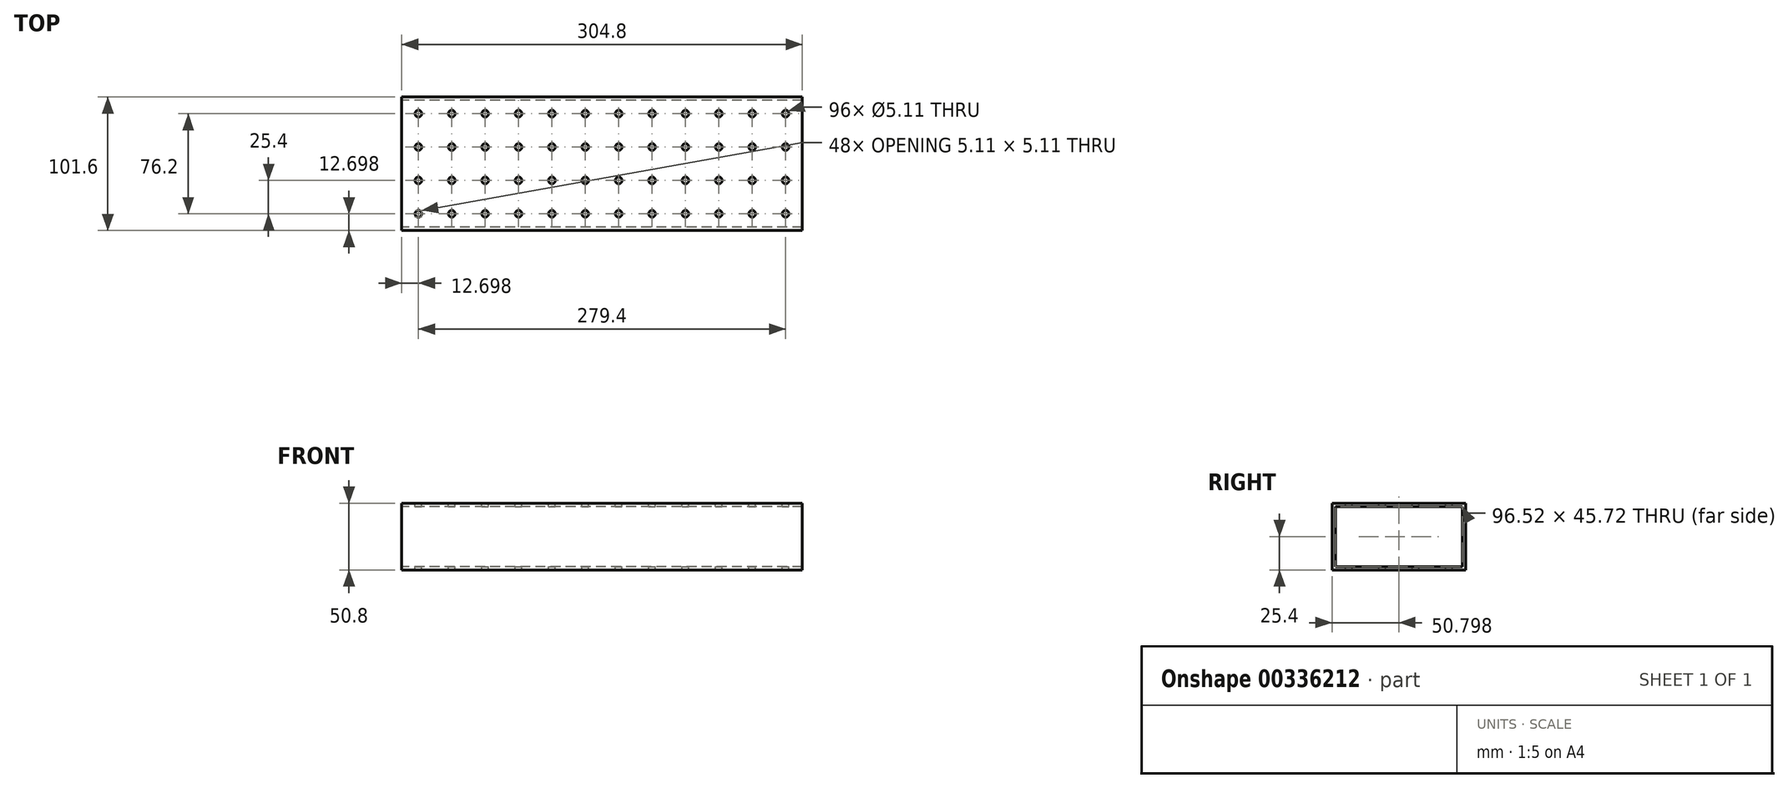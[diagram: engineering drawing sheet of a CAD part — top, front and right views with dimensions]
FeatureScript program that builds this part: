
annotation { "Feature Type Name" : "Feature", "Feature Type Description" : "" }
export const myFeature = defineFeature(function(context is Context, id is Id, definition is map)
    precondition{}
    {
        {
            var Q0;
            Q0=qCreatedBy(makeId("Top.planeOp"),FACE);
            var sketch = newSketch(context, id + "F0", { "sketchPlane" : qUnion([Q0])});
            skLineSegment(sketch, "E0.bottom", {"start": v(-146.87, 30.52) * mm, "end": v(157.93, 30.52) * mm});
            skLineSegment(sketch, "E0.top", {"start": v(-146.87, -71.08) * mm, "end": v(157.93, -71.08) * mm});
            skLineSegment(sketch, "E0.left", {"start": v(-146.87, 30.52) * mm, "end": v(-146.87, -71.08) * mm});
            skLineSegment(sketch, "E0.right", {"start": v(157.93, 30.52) * mm, "end": v(157.93, -71.08) * mm});
            skSolve(sketch);
        }
        {
            var Q0;
            Q0 = qSketchRegion(id + "F0", true);
            extrude(context, id + "F1", {"entities" : qUnion([Q0]), "depth" : 50.8 * mm});
        }
        {
            var Q0;
            Q0=makeQuery(id+"F1.opExtrude","SWEPT_FACE",FACE,{"disambiguationData":[OSD([sQuery(id+"F0.wireOp",EDGE,"E0.left")])]});
            var sketch = newSketch(context, id + "F2", { "sketchPlane" : qUnion([Q0])});
            skLineSegment(sketch, "E1.bottom", {"start": v(-27.98, 48.26) * mm, "end": v(68.54, 48.26) * mm});
            skLineSegment(sketch, "E1.top", {"start": v(-27.98, 2.54) * mm, "end": v(68.54, 2.54) * mm});
            skLineSegment(sketch, "E1.left", {"start": v(-27.98, 48.26) * mm, "end": v(-27.98, 2.54) * mm});
            skLineSegment(sketch, "E1.right", {"start": v(68.54, 48.26) * mm, "end": v(68.54, 2.54) * mm});
            skSolve(sketch);
        }
        {
            var Q0;
            Q0 = qSketchRegion(id + "F2", true);
            extrude(context, id + "F3", {"entities" : qUnion([Q0]), "operationType" : NewBodyOperationType.REMOVE, "endBound" : BoundingType.THROUGH_ALL, "oppositeDirection" : true, "depth" : 25.4 * mm});
        }
        {
            var Q0;
            Q0=makeQuery(id+"F1.opExtrude","CAP_FACE",FACE,{"disambiguationData":[OSD([sQuery(id+"F0.wireOp",EDGE,"E0.bottom"),sQuery(id+"F0.wireOp",EDGE,"E0.top"),sQuery(id+"F0.wireOp",EDGE,"E0.left"),sQuery(id+"F0.wireOp",EDGE,"E0.right")])],"isStart":false});
            var sketch = newSketch(context, id + "F4", { "sketchPlane" : qUnion([Q0])});
            skCircle(sketch, "E2", {"center": v(-134.17, 17.82) * mm, "radius": 2.55 * mm});
            skCircle(sketch, "E3.0.1.0", {"center": v(-134.17, -7.58) * mm, "radius": 2.55 * mm});
            skCircle(sketch, "E3.0.2.0", {"center": v(-134.17, -32.98) * mm, "radius": 2.55 * mm});
            skCircle(sketch, "E3.0.3.0", {"center": v(-134.17, -58.38) * mm, "radius": 2.55 * mm});
            skCircle(sketch, "E3.1.0.0", {"center": v(-108.77, 17.82) * mm, "radius": 2.55 * mm});
            skCircle(sketch, "E3.1.1.0", {"center": v(-108.77, -7.58) * mm, "radius": 2.55 * mm});
            skCircle(sketch, "E3.1.2.0", {"center": v(-108.77, -32.98) * mm, "radius": 2.55 * mm});
            skCircle(sketch, "E3.1.3.0", {"center": v(-108.77, -58.38) * mm, "radius": 2.55 * mm});
            skCircle(sketch, "E3.2.0.0", {"center": v(-83.37, 17.82) * mm, "radius": 2.55 * mm});
            skCircle(sketch, "E3.2.1.0", {"center": v(-83.37, -7.58) * mm, "radius": 2.55 * mm});
            skCircle(sketch, "E3.2.2.0", {"center": v(-83.37, -32.98) * mm, "radius": 2.55 * mm});
            skCircle(sketch, "E3.2.3.0", {"center": v(-83.37, -58.38) * mm, "radius": 2.55 * mm});
            skCircle(sketch, "E3.3.0.0", {"center": v(-57.97, 17.82) * mm, "radius": 2.55 * mm});
            skCircle(sketch, "E3.3.1.0", {"center": v(-57.97, -7.58) * mm, "radius": 2.55 * mm});
            skCircle(sketch, "E3.3.2.0", {"center": v(-57.97, -32.98) * mm, "radius": 2.55 * mm});
            skCircle(sketch, "E3.3.3.0", {"center": v(-57.97, -58.38) * mm, "radius": 2.55 * mm});
            skCircle(sketch, "E3.4.0.0", {"center": v(-32.57, 17.82) * mm, "radius": 2.55 * mm});
            skCircle(sketch, "E3.4.1.0", {"center": v(-32.57, -7.58) * mm, "radius": 2.55 * mm});
            skCircle(sketch, "E3.4.2.0", {"center": v(-32.57, -32.98) * mm, "radius": 2.55 * mm});
            skCircle(sketch, "E3.4.3.0", {"center": v(-32.57, -58.38) * mm, "radius": 2.55 * mm});
            skCircle(sketch, "E3.5.0.0", {"center": v(-7.17, 17.82) * mm, "radius": 2.55 * mm});
            skCircle(sketch, "E3.5.1.0", {"center": v(-7.17, -7.58) * mm, "radius": 2.55 * mm});
            skCircle(sketch, "E3.5.2.0", {"center": v(-7.17, -32.98) * mm, "radius": 2.55 * mm});
            skCircle(sketch, "E3.5.3.0", {"center": v(-7.17, -58.38) * mm, "radius": 2.55 * mm});
            skCircle(sketch, "E3.6.0.0", {"center": v(18.23, 17.82) * mm, "radius": 2.55 * mm});
            skCircle(sketch, "E3.6.1.0", {"center": v(18.23, -7.58) * mm, "radius": 2.55 * mm});
            skCircle(sketch, "E3.6.2.0", {"center": v(18.23, -32.98) * mm, "radius": 2.55 * mm});
            skCircle(sketch, "E3.6.3.0", {"center": v(18.23, -58.38) * mm, "radius": 2.55 * mm});
            skCircle(sketch, "E3.7.0.0", {"center": v(43.63, 17.82) * mm, "radius": 2.55 * mm});
            skCircle(sketch, "E3.7.1.0", {"center": v(43.63, -7.58) * mm, "radius": 2.55 * mm});
            skCircle(sketch, "E3.7.2.0", {"center": v(43.63, -32.98) * mm, "radius": 2.55 * mm});
            skCircle(sketch, "E3.7.3.0", {"center": v(43.63, -58.38) * mm, "radius": 2.55 * mm});
            skCircle(sketch, "E3.8.0.0", {"center": v(69.03, 17.82) * mm, "radius": 2.55 * mm});
            skCircle(sketch, "E3.8.1.0", {"center": v(69.03, -7.58) * mm, "radius": 2.55 * mm});
            skCircle(sketch, "E3.8.2.0", {"center": v(69.03, -32.98) * mm, "radius": 2.55 * mm});
            skCircle(sketch, "E3.8.3.0", {"center": v(69.03, -58.38) * mm, "radius": 2.55 * mm});
            skCircle(sketch, "E3.9.0.0", {"center": v(94.43, 17.82) * mm, "radius": 2.55 * mm});
            skCircle(sketch, "E3.9.1.0", {"center": v(94.43, -7.58) * mm, "radius": 2.55 * mm});
            skCircle(sketch, "E3.9.2.0", {"center": v(94.43, -32.98) * mm, "radius": 2.55 * mm});
            skCircle(sketch, "E3.9.3.0", {"center": v(94.43, -58.38) * mm, "radius": 2.55 * mm});
            skCircle(sketch, "E3.10.0.0", {"center": v(119.83, 17.82) * mm, "radius": 2.55 * mm});
            skCircle(sketch, "E3.10.1.0", {"center": v(119.83, -7.58) * mm, "radius": 2.55 * mm});
            skCircle(sketch, "E3.10.2.0", {"center": v(119.83, -32.98) * mm, "radius": 2.55 * mm});
            skCircle(sketch, "E3.10.3.0", {"center": v(119.83, -58.38) * mm, "radius": 2.55 * mm});
            skCircle(sketch, "E3.11.0.0", {"center": v(145.23, 17.82) * mm, "radius": 2.55 * mm});
            skCircle(sketch, "E3.11.1.0", {"center": v(145.23, -7.58) * mm, "radius": 2.55 * mm});
            skCircle(sketch, "E3.11.2.0", {"center": v(145.23, -32.98) * mm, "radius": 2.55 * mm});
            skCircle(sketch, "E3.11.3.0", {"center": v(145.23, -58.38) * mm, "radius": 2.55 * mm});
            skLineSegment(sketch, "E3.direction1", {"start": v(-134.17, 17.82) * mm, "end": v(-108.77, 17.82) * mm, "construction": true});
            skLineSegment(sketch, "E3.direction2", {"start": v(-134.17, 17.82) * mm, "end": v(-134.17, -7.58) * mm, "construction": true});
            skSolve(sketch);
        }
        {
            var Q0;
            Q0=sQuery(id+"F4.wireOp",VERTEX,"E3.11.3.0.center");
            var Q1;
            Q1=sQuery(id+"F4.wireOp",VERTEX,"E3.7.3.0.center");
            var Q2;
            Q2=sQuery(id+"F4.wireOp",VERTEX,"E3.3.3.0.center");
            var Q3;
            Q3=sQuery(id+"F4.wireOp",VERTEX,"E3.9.2.0.center");
            var Q4;
            Q4=sQuery(id+"F4.wireOp",VERTEX,"E3.5.2.0.center");
            var Q5;
            Q5=sQuery(id+"F4.wireOp",VERTEX,"E3.10.1.0.center");
            var Q6;
            Q6=sQuery(id+"F4.wireOp",VERTEX,"E3.8.0.0.center");
            var Q7;
            Q7=sQuery(id+"F4.wireOp",VERTEX,"E3.6.1.0.center");
            var Q8;
            Q8=sQuery(id+"F4.wireOp",VERTEX,"E3.4.0.0.center");
            var Q9;
            Q9=sQuery(id+"F4.wireOp",VERTEX,"E3.8.3.0.center");
            var Q10;
            Q10=sQuery(id+"F4.wireOp",VERTEX,"E3.4.3.0.center");
            var Q11;
            Q11=sQuery(id+"F4.wireOp",VERTEX,"E3.11.0.0.center");
            var Q12;
            Q12=sQuery(id+"F4.wireOp",VERTEX,"E3.7.0.0.center");
            var Q13;
            Q13=sQuery(id+"F4.wireOp",VERTEX,"E3.3.0.0.center");
            var Q14;
            Q14=sQuery(id+"F4.wireOp",VERTEX,"E3.9.3.0.center");
            var Q15;
            Q15=sQuery(id+"F4.wireOp",VERTEX,"E3.5.3.0.center");
            var Q16;
            Q16=sQuery(id+"F4.wireOp",VERTEX,"E3.10.2.0.center");
            var Q17;
            Q17=sQuery(id+"F4.wireOp",VERTEX,"E3.8.1.0.center");
            var Q18;
            Q18=sQuery(id+"F4.wireOp",VERTEX,"E3.6.2.0.center");
            var Q19;
            Q19=sQuery(id+"F4.wireOp",VERTEX,"E3.4.1.0.center");
            var Q20;
            Q20=sQuery(id+"F4.wireOp",VERTEX,"E3.11.1.0.center");
            var Q21;
            Q21=sQuery(id+"F4.wireOp",VERTEX,"E3.7.1.0.center");
            var Q22;
            Q22=sQuery(id+"F4.wireOp",VERTEX,"E3.3.1.0.center");
            var Q23;
            Q23=sQuery(id+"F4.wireOp",VERTEX,"E3.10.0.0.center");
            var Q24;
            Q24=sQuery(id+"F4.wireOp",VERTEX,"E3.2.1.0.center");
            var Q25;
            Q25=sQuery(id+"F4.wireOp",VERTEX,"E3.6.0.0.center");
            var Q26;
            Q26=sQuery(id+"F4.wireOp",VERTEX,"E3.2.2.0.center");
            var Q27;
            Q27=sQuery(id+"F4.wireOp",VERTEX,"E3.2.3.0.center");
            var Q28;
            Q28=sQuery(id+"F4.wireOp",VERTEX,"E3.9.0.0.center");
            var Q29;
            Q29=sQuery(id+"F4.wireOp",VERTEX,"E3.5.0.0.center");
            var Q30;
            Q30=sQuery(id+"F4.wireOp",VERTEX,"E2.center");
            var Q31;
            Q31=sQuery(id+"F4.wireOp",VERTEX,"E3.10.3.0.center");
            var Q32;
            Q32=sQuery(id+"F4.wireOp",VERTEX,"E3.6.3.0.center");
            var Q33;
            Q33=sQuery(id+"F4.wireOp",VERTEX,"E3.8.2.0.center");
            var Q34;
            Q34=sQuery(id+"F4.wireOp",VERTEX,"E3.4.2.0.center");
            var Q35;
            Q35=sQuery(id+"F4.wireOp",VERTEX,"E3.0.1.0.center");
            var Q36;
            Q36=sQuery(id+"F4.wireOp",VERTEX,"E3.0.2.0.center");
            var Q37;
            Q37=sQuery(id+"F4.wireOp",VERTEX,"E3.11.2.0.center");
            var Q38;
            Q38=sQuery(id+"F4.wireOp",VERTEX,"E3.7.2.0.center");
            var Q39;
            Q39=sQuery(id+"F4.wireOp",VERTEX,"E3.0.3.0.center");
            var Q40;
            Q40=sQuery(id+"F4.wireOp",VERTEX,"E3.3.2.0.center");
            var Q41;
            Q41=sQuery(id+"F4.wireOp",VERTEX,"E3.1.0.0.center");
            var Q42;
            Q42=sQuery(id+"F4.wireOp",VERTEX,"E3.1.1.0.center");
            var Q43;
            Q43=sQuery(id+"F4.wireOp",VERTEX,"E3.1.2.0.center");
            var Q44;
            Q44=sQuery(id+"F4.wireOp",VERTEX,"E3.1.3.0.center");
            var Q45;
            Q45=sQuery(id+"F4.wireOp",VERTEX,"E3.2.0.0.center");
            var Q46;
            Q46=sQuery(id+"F4.wireOp",VERTEX,"E3.9.1.0.center");
            var Q47;
            Q47=sQuery(id+"F4.wireOp",VERTEX,"E3.5.1.0.center");
            var Q48;
            Q48=makeQuery(id+"F1.opExtrude","SWEPT_BODY",BODY,{"disambiguationData":[OSD([sQuery(id+"F0.wireOp",EDGE,"E0.bottom"),sQuery(id+"F0.wireOp",EDGE,"E0.top"),sQuery(id+"F0.wireOp",EDGE,"E0.left"),sQuery(id+"F0.wireOp",EDGE,"E0.right")])]});
            hole(context, id + "F5", {"style" : HoleStyle.SIMPLE, "endStyle" : HoleEndStyle.THROUGH, "holeDiameter" : 5.1 * mm, "tappedDepth" : 12.7 * mm, "tapClearance" : 3, "locations" : qUnion([Q0, Q1, Q2, Q3, Q4, Q5, Q6, Q7, Q8, Q9, Q10, Q11, Q12, Q13, Q14, Q15, Q16, Q17, Q18, Q19, Q20, Q21, Q22, Q23, Q24, Q25, Q26, Q27, Q28, Q29, Q30, Q31, Q32, Q33, Q34, Q35, Q36, Q37, Q38, Q39, Q40, Q41, Q42, Q43, Q44, Q45, Q46, Q47]), "scope" : qUnion([Q48])});
        }
    });
